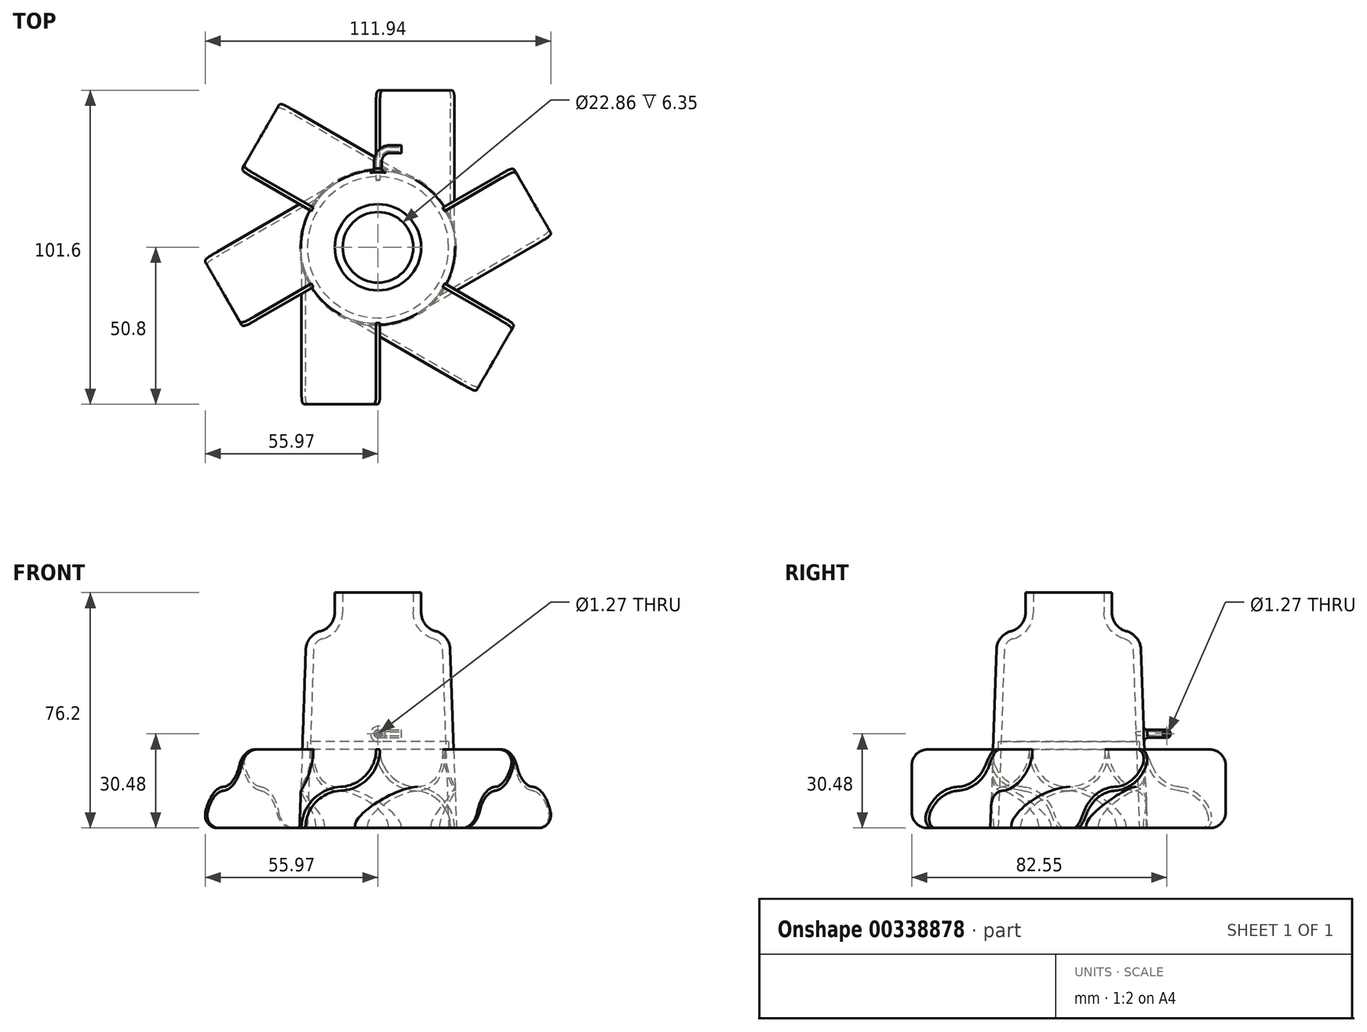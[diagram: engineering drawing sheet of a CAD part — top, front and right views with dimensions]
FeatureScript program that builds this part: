
annotation { "Feature Type Name" : "Feature", "Feature Type Description" : "" }
export const myFeature = defineFeature(function(context is Context, id is Id, definition is map)
    precondition{}
    {
        {
            var Q0;
            Q0=qCreatedBy(makeId("Front.planeOp"),FACE);
            var sketch = newSketch(context, id + "F0", { "sketchPlane" : qUnion([Q0])});
            skLineSegment(sketch, "E0.right", {"start": v(25.4, 0) * mm, "end": v(23.38, 57.8) * mm});
            skArc(sketch, "E1", {"start": v(23.38, 57.8) * mm, "mid": v(22, 61.54) * mm, "end": v(18.68, 63.72) * mm});
            skLineSegment(sketch, "E2", {"start": v(13.97, 76.2) * mm, "end": v(13.97, 69.85) * mm});
            skArc(sketch, "E3", {"start": v(13.97, 69.85) * mm, "mid": v(15.28, 65.98) * mm, "end": v(18.68, 63.72) * mm});
            skLineSegment(sketch, "E4", {"start": v(18.68, 63.72) * mm, "end": v(0, 68.72) * mm, "construction": true});
            skLineSegment(sketch, "E5.0", {"start": v(22.86, 0) * mm, "end": v(20.84, 57.72) * mm});
            skArc(sketch, "E6.0", {"start": v(11.43, 69.85) * mm, "mid": v(13.27, 64.44) * mm, "end": v(18.02, 61.26) * mm});
            skArc(sketch, "E7.0", {"start": v(20.84, 57.72) * mm, "mid": v(20.01, 59.95) * mm, "end": v(18.02, 61.26) * mm});
            skPoint(sketch, "E8.startSnap0", {"position": v(15.28, 65.98) * mm});
            skLineSegment(sketch, "E9", {"start": v(11.43, 69.85) * mm, "end": v(11.43, 76.2) * mm});
            skLineSegment(sketch, "E10", {"start": v(11.43, 76.2) * mm, "end": v(13.97, 76.2) * mm});
            skLineSegment(sketch, "E11", {"start": v(22.86, 0) * mm, "end": v(25.4, 0) * mm});
            skLineSegment(sketch, "E12", {"start": v(0, -2.44) * mm, "end": v(0, 68.72) * mm, "construction": true});
            skSolve(sketch);
        }
        {
            var Q0;
            Q0=makeQuery(id+"F0.imprint","IMPRINT",FACE,{"disambiguationData":[TD([[makeQuery(id+"F0.imprint","IMPRINT",EDGE,{"derivedFrom":sQuery(id+"F0.wireOp",EDGE,"E0.right")}),1.0]])]});
            var Q1;
            Q1=sQuery(id+"F0.wireOp",EDGE,"E12");
            revolve(context, id + "F1", {"entities" : qUnion([Q0]), "axis" : qUnion([Q1]), "revolveType" : RevolveType.FULL});
        }
        {
            var Q0;
            Q0=qCreatedBy(makeId("Top.planeOp"),FACE);
            var sketch = newSketch(context, id + "F2", { "sketchPlane" : qUnion([Q0])});
            skCircle(sketch, "E13", {"center": v(0, 0) * mm, "radius": 22.86 * mm});
            skSolve(sketch);
        }
        {
            var Q0;
            Q0 = qSketchRegion(id + "F2", true);
            extrude(context, id + "F3", {"entities" : qUnion([Q0]), "depth" : 2.54 * mm});
        }
        {
            var Q0;
            Q0=makeQuery(id+"F3.opExtrude","SWEPT_BODY",BODY,{"disambiguationData":[OSD([sQuery(id+"F2.wireOp",EDGE,"E13")])]});
            var Q1;
            Q1=makeQuery(id+"F3.opExtrude","CAP_FACE",FACE,{"disambiguationData":[OSD([sQuery(id+"F2.wireOp",EDGE,"E13")])],"isStart":true});
            transform(context, id + "F4", {"entities" : qUnion([Q0]), "transformType" : TransformType.TRANSLATION_DISTANCE, "transformDirection" : qUnion([Q1]), "distance" : 25.4 * mm, "oppositeDirection" : true, "makeCopy" : false});
        }
        {
            var Q0;
            Q0=qCreatedBy(makeId("Front.planeOp"),FACE);
            cPlane(context, id + "F5", {"entities" : qUnion([Q0]), "cplaneType" : CPlaneType.OFFSET, "offset" : 50.8 * mm, "width" : 152.4 * mm, "height" : 152.4 * mm});
        }
        {
            var Q0;
            Q0=qCreatedBy(id+"F5.planeOp",FACE);
            var sketch = newSketch(context, id + "F6", { "sketchPlane" : qUnion([Q0])});
            skArc(sketch, "E14", {"start": v(-12.06, 12.7) * mm, "mid": v(-3.5, 16.64) * mm, "end": v(0, 25.4) * mm, "construction": true});
            skArc(sketch, "E15", {"start": v(-12.06, 12.7) * mm, "mid": v(-20.63, 8.76) * mm, "end": v(-24.13, 0) * mm, "construction": true});
            skLineSegment(sketch, "E16", {"start": v(0, 25.4) * mm, "end": v(-24.13, 0) * mm, "construction": true});
            skLineSegment(sketch, "E17", {"start": v(0, 25.4) * mm, "end": v(0, 0) * mm, "construction": true});
            skLineSegment(sketch, "E18", {"start": v(0, 0) * mm, "end": v(-24.13, 0) * mm, "construction": true});
            skArc(sketch, "E19.0.startCap", {"start": v(-12.03, 12.07) * mm, "mid": v(-12.7, 12.67) * mm, "end": v(-12.1, 13.33) * mm, "construction": true});
            skArc(sketch, "E19.0.endCap", {"start": v(-0.64, 25.4) * mm, "mid": v(0, 26.04) * mm, "end": v(0.64, 25.4) * mm, "construction": true});
            skArc(sketch, "E19.0.left", {"start": v(-12.1, 13.33) * mm, "mid": v(-3.96, 17.08) * mm, "end": v(-0.63, 25.4) * mm});
            skArc(sketch, "E19.0.right", {"start": v(-12.03, 12.07) * mm, "mid": v(-3.04, 16.2) * mm, "end": v(0.63, 25.4) * mm});
            skArc(sketch, "E19.1.startCap", {"start": v(-12.1, 13.33) * mm, "mid": v(-11.43, 12.73) * mm, "end": v(-12.03, 12.07) * mm, "construction": true});
            skArc(sketch, "E19.1.endCap", {"start": v(-23.5, 0) * mm, "mid": v(-24.13, -0.64) * mm, "end": v(-24.77, 0) * mm, "construction": true});
            skArc(sketch, "E19.1.left", {"start": v(-12.03, 12.07) * mm, "mid": v(-20.17, 8.32) * mm, "end": v(-23.5, 0) * mm});
            skArc(sketch, "E19.1.right", {"start": v(-12.1, 13.33) * mm, "mid": v(-21.1, 9.2) * mm, "end": v(-24.76, 0) * mm});
            skLineSegment(sketch, "E20", {"start": v(-0.63, 25.4) * mm, "end": v(0.63, 25.4) * mm});
            skLineSegment(sketch, "E21", {"start": v(-24.77, 0) * mm, "end": v(-23.5, 0) * mm});
            skSolve(sketch);
        }
        {
            var Q0;
            Q0 = qSketchRegion(id + "F6", true);
            extrude(context, id + "F7", {"entities" : qUnion([Q0]), "endBound" : BoundingType.UP_TO_NEXT, "oppositeDirection" : true, "depth" : 25.4 * mm});
        }
        {
            var Q0;
            Q0=makeQuery(id+"F7.opExtrude","SWEPT_BODY",BODY,{"disambiguationData":[OSD([sQuery(id+"F6.wireOp",EDGE,"E19.0.left"),sQuery(id+"F6.wireOp",EDGE,"E19.0.right"),sQuery(id+"F6.wireOp",EDGE,"E19.1.left"),sQuery(id+"F6.wireOp",EDGE,"E19.1.right"),sQuery(id+"F6.wireOp",EDGE,"E20"),sQuery(id+"F6.wireOp",EDGE,"E21")])]});
            var Q1;
            Q1=makeQuery(id+"F1.opRevolve","SWEPT_FACE",FACE,{"disambiguationData":[OSD([sQuery(id+"F0.wireOp",EDGE,"E0.right")])]});
            circularPattern(context, id + "F8", {"entities" : qUnion([Q0]), "axis" : qUnion([Q1]), "angle" : 360 * degree, "instanceCount" : 6, "equalSpace" : true});
        }
        {
            var Q0;
            Q0=qCreatedBy(makeId("Top.planeOp"),FACE);
            cPlane(context, id + "F9", {"entities" : qUnion([Q0]), "cplaneType" : CPlaneType.OFFSET, "offset" : 30.48 * mm, "width" : 152.4 * mm, "height" : 152.4 * mm});
        }
        {
            var Q0;
            Q0=qCreatedBy(id+"F9.planeOp",FACE);
            var sketch = newSketch(context, id + "F10", { "sketchPlane" : qUnion([Q0])});
            skLineSegment(sketch, "E22", {"start": v(0, 0) * mm, "end": v(0, 24.13) * mm, "construction": true});
            skLineSegment(sketch, "E23", {"start": v(3.8, 31.75) * mm, "end": v(7.62, 31.75) * mm});
            skArc(sketch, "E24.filletArc", {"start": v(3.81, 31.75) * mm, "mid": v(1.12, 30.63) * mm, "end": v(0, 27.94) * mm});
            skLineSegment(sketch, "E25", {"start": v(0, 24.13) * mm, "end": v(0, 27.94) * mm});
            skSolve(sketch);
        }
        {
            var Q0;
            Q0=qCreatedBy(makeId("Front.planeOp"),FACE);
            var sketch = newSketch(context, id + "F11", { "sketchPlane" : qUnion([Q0])});
            skCircle(sketch, "E26", {"center": v(0, 30.48) * mm, "radius": 0.64 * mm});
            skSolve(sketch);
        }
        {
            var Q0;
            Q0 = qSketchRegion(id + "F11", true);
            extrude(context, id + "F12", {"entities" : qUnion([Q0]), "operationType" : NewBodyOperationType.REMOVE, "oppositeDirection" : true, "depth" : 50.8 * mm});
        }
        {
            var Q0;
            Q0=qCreatedBy(makeId("Front.planeOp"),FACE);
            cPlane(context, id + "F13", {"entities" : qUnion([Q0]), "cplaneType" : CPlaneType.OFFSET, "offset" : 24.13 * mm, "oppositeDirection" : true, "width" : 152.4 * mm, "height" : 152.4 * mm});
        }
        {
            var Q0;
            Q0=qCreatedBy(id+"F13.planeOp",FACE);
            var sketch = newSketch(context, id + "F14", { "sketchPlane" : qUnion([Q0])});
            skCircle(sketch, "E27", {"center": v(0, 30.48) * mm, "radius": 1.27 * mm});
            skCircle(sketch, "E28", {"center": v(0, 30.48) * mm, "radius": 0.64 * mm});
            skSolve(sketch);
        }
        {
            var Q0;
            Q0 = qSketchRegion(id + "F14", true);
            var Q1;
            Q1 = qConstructionFilter(qBodyType(qCreatedBy(id + "F10" ,EDGE), BodyType.WIRE), ConstructionObject.NO);
            sweep(context, id + "F15", {"operationType" : NewBodyOperationType.ADD, "profiles" : qUnion([Q0]), "path" : qUnion([Q1])});
        }
        {
            var Q0;
            Q0=makeQuery(id+"F8.opPattern","COPY",EDGE,{"derivedFrom":makeQuery(id+"F7.opExtrude","CAP_EDGE",EDGE,{"disambiguationData":[OSD([sQuery(id+"F6.wireOp",EDGE,"E20")])],"isStart":true}),"instanceName":"1"});
            var Q1;
            Q1=makeQuery(id+"F8.opPattern","COPY",EDGE,{"derivedFrom":makeQuery(id+"F7.opExtrude","CAP_EDGE",EDGE,{"disambiguationData":[OSD([sQuery(id+"F6.wireOp",EDGE,"E21")])],"isStart":true}),"instanceName":"1"});
            var Q2;
            Q2=makeQuery(id+"F7.opExtrude","CAP_EDGE",EDGE,{"disambiguationData":[OSD([sQuery(id+"F6.wireOp",EDGE,"E21")])],"isStart":true});
            var Q3;
            Q3=makeQuery(id+"F7.opExtrude","CAP_EDGE",EDGE,{"disambiguationData":[OSD([sQuery(id+"F6.wireOp",EDGE,"E20")])],"isStart":true});
            var Q4;
            Q4=makeQuery(id+"F8.opPattern","COPY",EDGE,{"derivedFrom":makeQuery(id+"F7.opExtrude","CAP_EDGE",EDGE,{"disambiguationData":[OSD([sQuery(id+"F6.wireOp",EDGE,"E21")])],"isStart":true}),"instanceName":"5"});
            var Q5;
            Q5=makeQuery(id+"F8.opPattern","COPY",EDGE,{"derivedFrom":makeQuery(id+"F7.opExtrude","CAP_EDGE",EDGE,{"disambiguationData":[OSD([sQuery(id+"F6.wireOp",EDGE,"E20")])],"isStart":true}),"instanceName":"5"});
            var Q6;
            Q6=makeQuery(id+"F8.opPattern","COPY",EDGE,{"derivedFrom":makeQuery(id+"F7.opExtrude","CAP_EDGE",EDGE,{"disambiguationData":[OSD([sQuery(id+"F6.wireOp",EDGE,"E21")])],"isStart":true}),"instanceName":"4"});
            var Q7;
            Q7=makeQuery(id+"F8.opPattern","COPY",EDGE,{"derivedFrom":makeQuery(id+"F7.opExtrude","CAP_EDGE",EDGE,{"disambiguationData":[OSD([sQuery(id+"F6.wireOp",EDGE,"E20")])],"isStart":true}),"instanceName":"4"});
            var Q8;
            Q8=makeQuery(id+"F8.opPattern","COPY",EDGE,{"derivedFrom":makeQuery(id+"F7.opExtrude","CAP_EDGE",EDGE,{"disambiguationData":[OSD([sQuery(id+"F6.wireOp",EDGE,"E21")])],"isStart":true}),"instanceName":"3"});
            var Q9;
            Q9=makeQuery(id+"F8.opPattern","COPY",EDGE,{"derivedFrom":makeQuery(id+"F7.opExtrude","CAP_EDGE",EDGE,{"disambiguationData":[OSD([sQuery(id+"F6.wireOp",EDGE,"E20")])],"isStart":true}),"instanceName":"3"});
            var Q10;
            Q10=makeQuery(id+"F8.opPattern","COPY",EDGE,{"derivedFrom":makeQuery(id+"F7.opExtrude","CAP_EDGE",EDGE,{"disambiguationData":[OSD([sQuery(id+"F6.wireOp",EDGE,"E21")])],"isStart":true}),"instanceName":"2"});
            var Q11;
            Q11=makeQuery(id+"F8.opPattern","COPY",EDGE,{"derivedFrom":makeQuery(id+"F7.opExtrude","CAP_EDGE",EDGE,{"disambiguationData":[OSD([sQuery(id+"F6.wireOp",EDGE,"E20")])],"isStart":true}),"instanceName":"2"});
            fillet(context, id + "F16", {"entities" : qUnion([Q0, Q1, Q2, Q3, Q4, Q5, Q6, Q7, Q8, Q9, Q10, Q11]), "radius" : 5.08 * mm, "tangentPropagation" : true, "allowEdgeOverflow" : false});
        }
        {
            var Q0;
            Q0=makeQuery(id+"F15.boolean.opBoolean","INTERSECT",EDGE,{"derivedFrom":[makeQuery(id+"F1.opRevolve","SWEPT_FACE",FACE,{"disambiguationData":[OSD([sQuery(id+"F0.wireOp",EDGE,"E0.right")])]}),makeQuery(id+"F15.opSweep","SWEPT_FACE",FACE,{"disambiguationData":[OSD([sQuery(id+"F10.wireOp",EDGE,"E25"),sQuery(id+"F14.wireOp",EDGE,"E27")])]})]});
            fillet(context, id + "F17", {"entities" : qUnion([Q0]), "radius" : 1.27 * mm, "tangentPropagation" : true, "allowEdgeOverflow" : false});
        }
    });
